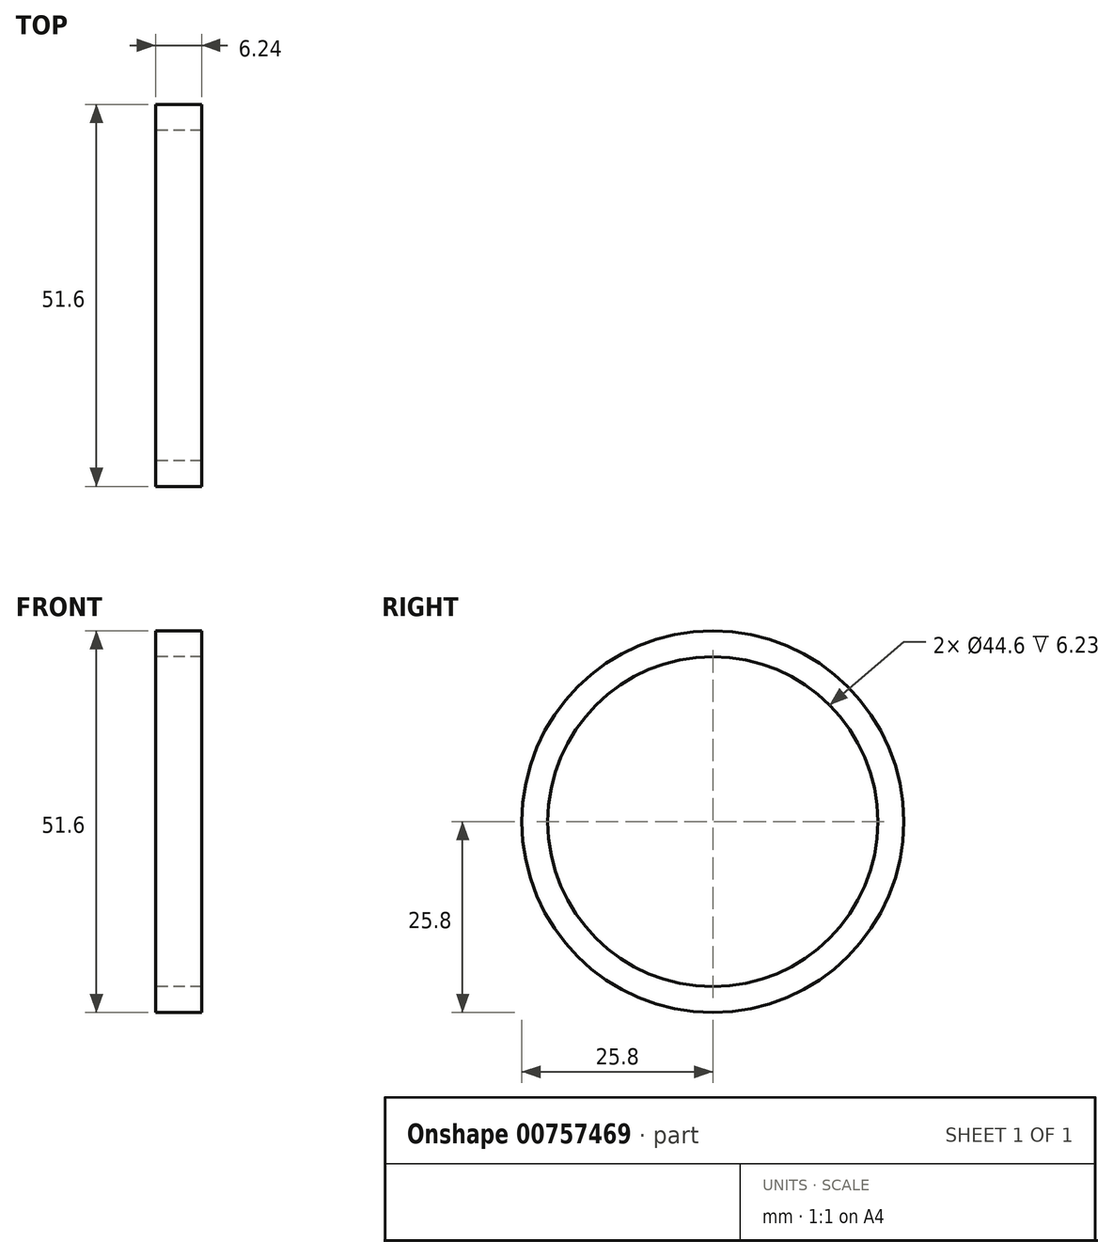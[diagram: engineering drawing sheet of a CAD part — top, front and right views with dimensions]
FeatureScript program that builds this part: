
annotation { "Feature Type Name" : "Feature", "Feature Type Description" : "" }
export const myFeature = defineFeature(function(context is Context, id is Id, definition is map)
    precondition{}
    {
        {
            var Q0;
            Q0=qCreatedBy(makeId("Right.planeOp"),FACE);
            var sketch = newSketch(context, id + "F0", { "sketchPlane" : qUnion([Q0])});
            skCircle(sketch, "E0", {"center": v(0, 0) * mm, "radius": 25.8 * mm});
            skCircle(sketch, "E1", {"center": v(0, 0) * mm, "radius": 22.3 * mm});
            skSolve(sketch);
        }
        {
            var Q0;
            Q0 = qSketchRegion(id + "F0", true);
            extrude(context, id + "F1", {"entities" : qUnion([Q0]), "endBound" : BoundingType.SYMMETRIC, "depth" : 6.23 * mm, "offsetDistance" : 25 * mm});
        }
    });
